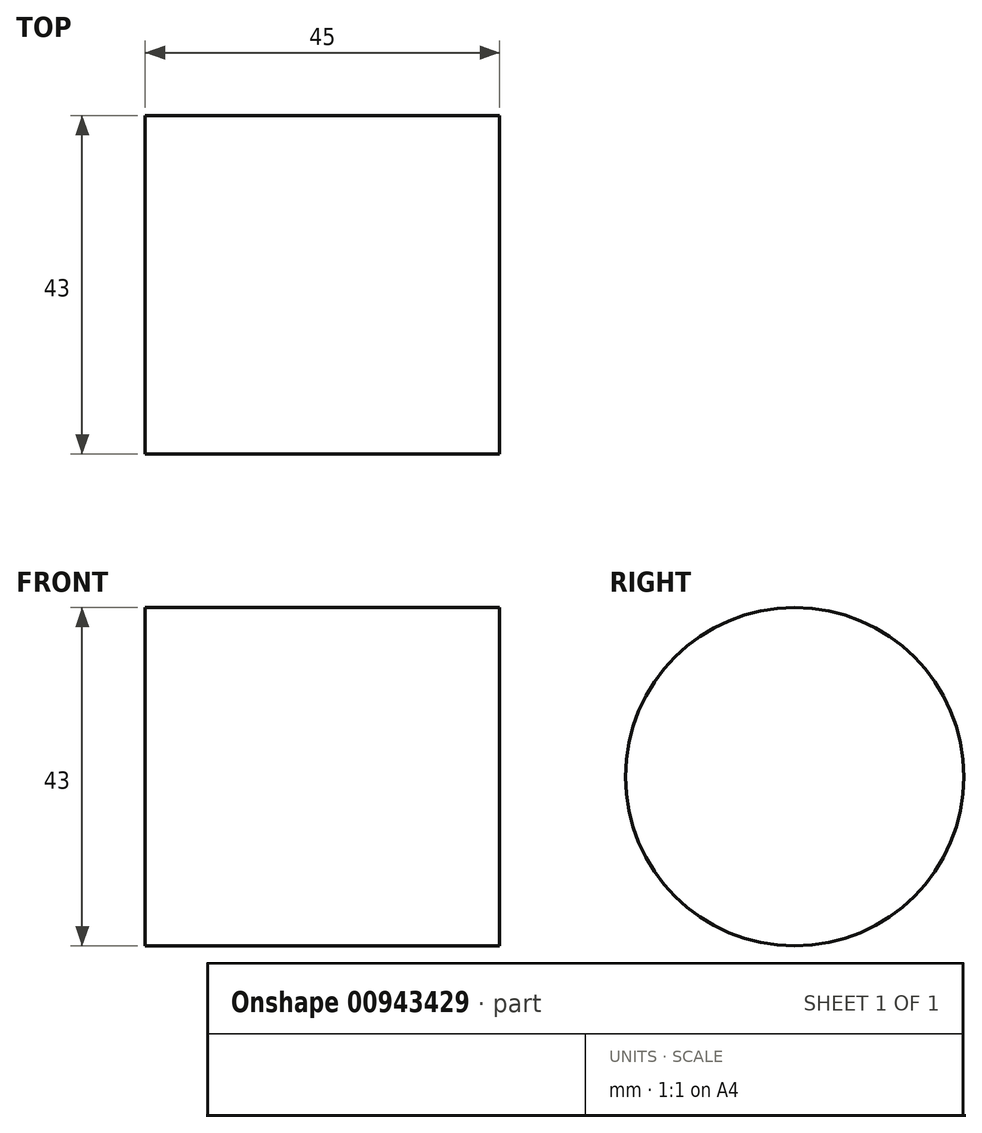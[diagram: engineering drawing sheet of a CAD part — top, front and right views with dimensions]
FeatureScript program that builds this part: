
annotation { "Feature Type Name" : "Feature", "Feature Type Description" : "" }
export const myFeature = defineFeature(function(context is Context, id is Id, definition is map)
    precondition{}
    {
        {
            var Q0;
            Q0=qCreatedBy(makeId("Right.planeOp"),FACE);
            var sketch = newSketch(context, id + "F0", { "sketchPlane" : qUnion([Q0])});
            skCircle(sketch, "E0", {"center": v(0, 0) * mm, "radius": 21.5 * mm});
            skSolve(sketch);
        }
        {
            var Q0;
            Q0 = qSketchRegion(id + "F0", true);
            extrude(context, id + "F1", {"entities" : qUnion([Q0]), "depth" : 45 * mm, "offsetDistance" : 25.4 * mm});
        }
    });
